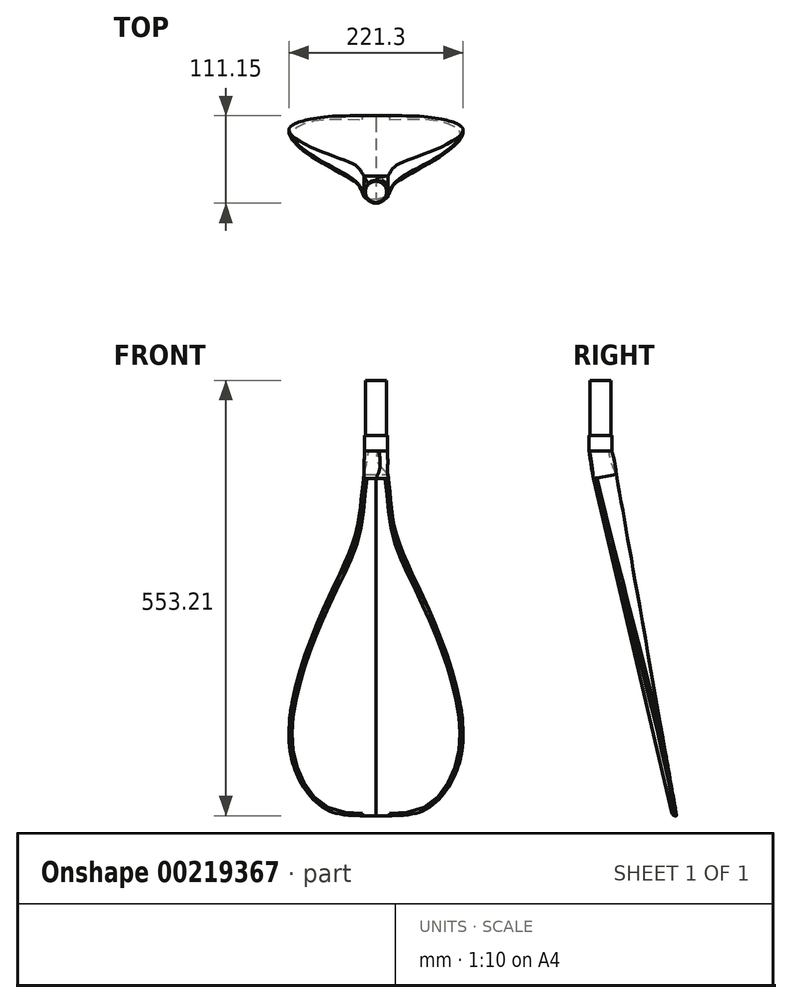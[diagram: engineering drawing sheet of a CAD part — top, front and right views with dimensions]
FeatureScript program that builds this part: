
annotation { "Feature Type Name" : "Feature", "Feature Type Description" : "" }
export const myFeature = defineFeature(function(context is Context, id is Id, definition is map)
    precondition{}
    {
        {
            var Q0;
            Q0=qCreatedBy(makeId("Top.planeOp"),FACE);
            cPlane(context, id + "F0", {"entities" : qUnion([Q0]), "cplaneType" : CPlaneType.OFFSET, "offset" : 500 * mm, "width" : 150 * mm, "height" : 150 * mm});
        }
        {
            var Q0;
            Q0=qCreatedBy(id+"F0.planeOp",FACE);
            var sketch = newSketch(context, id + "F1", { "sketchPlane" : qUnion([Q0])});
            skCircle(sketch, "E0", {"center": v(0, 0) * mm, "radius": 14.5 * mm});
            skSolve(sketch);
        }
        {
            var Q0;
            Q0 = qSketchRegion(id + "F1", true);
            extrude(context, id + "F2", {"entities" : qUnion([Q0]), "oppositeDirection" : true, "depth" : 20 * mm});
        }
        {
            var Q0;
            Q0=qCreatedBy(makeId("Right.planeOp"),FACE);
            var sketch = newSketch(context, id + "F3", { "sketchPlane" : qUnion([Q0])});
            skLineSegment(sketch, "E1", {"start": v(0, 500) * mm, "end": v(0, 450) * mm});
            skLineSegment(sketch, "E2", {"start": v(0, 450) * mm, "end": v(79.35, 0) * mm});
            skSolve(sketch);
        }
        {
            var Q0;
            Q0=sQuery(id+"F3.wireOp",EDGE,"E2");
            cPlane(context, id + "F4", {"entities" : qUnion([Q0]), "cplaneType" : CPlaneType.LINE_ANGLE, "offset" : 25 * mm, "angle" : 90 * degree, "width" : 150 * mm, "height" : 150 * mm});
        }
        {
            var Q0;
            Q0=qCreatedBy(id+"F4.planeOp",FACE);
            var sketch = newSketch(context, id + "F5", { "sketchPlane" : qUnion([Q0])});
            skLineSegment(sketch, "E3.bottom", {"start": v(115, 440) * mm, "end": v(-115, 440) * mm});
            skLineSegment(sketch, "E3.top", {"start": v(115, 0) * mm, "end": v(-115, 0) * mm});
            skLineSegment(sketch, "E3.left", {"start": v(115, 440) * mm, "end": v(115, 0) * mm});
            skLineSegment(sketch, "E3.right", {"start": v(-115, 440) * mm, "end": v(-115, 0) * mm});
            skSolve(sketch);
        }
        {
            var Q0;
            Q0=makeQuery(id+"F5.imprint","IMPRINT",FACE,{"disambiguationData":[TD([[makeQuery(id+"F5.imprint","IMPRINT",EDGE,{"derivedFrom":sQuery(id+"F5.wireOp",EDGE,"E3.bottom")}),1.0]])]});
            extrude(context, id + "F6", {"entities" : qUnion([Q0]), "endBound" : BoundingType.SYMMETRIC, "depth" : 40 * mm});
        }
        {
            var Q0;
            Q0=makeQuery(id+"F6.opExtrude","CAP_FACE",FACE,{"disambiguationData":[OSD([sQuery(id+"F5.wireOp",EDGE,"E3.bottom"),sQuery(id+"F5.wireOp",EDGE,"E3.top"),sQuery(id+"F5.wireOp",EDGE,"E3.left"),sQuery(id+"F5.wireOp",EDGE,"E3.right")])],"isStart":false});
            var sketch = newSketch(context, id + "F7", { "sketchPlane" : qUnion([Q0])});
            skFitSpline(sketch, "E4", {"points": [v(0, 0) * mm, v(68.3, 10.67) * mm, v(110, 90.6) * mm, v(66.39, 268.32) * mm, v(26.77, 359.9) * mm, v(18, 415.25) * mm, v(15.5, 440) * mm], "startDerivative": vector(665.27, 0) * mm, "endDerivative": vector(0, 86.17) * mm});
            skFitSpline(sketch, "E5.MirrorCS", {"points": [v(0, 0) * mm, v(-68.3, 10.67) * mm, v(-110, 90.6) * mm, v(-66.39, 268.32) * mm, v(-26.77, 359.9) * mm, v(-18, 415.25) * mm, v(-15.5, 440) * mm], "startDerivative": vector(-665.27, 0) * mm, "endDerivative": vector(0, 86.17) * mm});
            skSolve(sketch);
        }
        {
            var Q0;
            {var subQ5=makeQuery(id+"F6.opExtrude","CAP_EDGE",EDGE,{"disambiguationData":[OSD([sQuery(id+"F5.wireOp",EDGE,"E3.left")])],"isStart":false});Q0=makeQuery(id+"F7.imprint","IMPRINT",FACE,{"disambiguationData":[TD([[makeQuery(id+"F7.imprint","IMPRINT",EDGE,{"derivedFrom":subQ5}),-1.0]])]});}
            var Q1;
            {var subQ5=makeQuery(id+"F6.opExtrude","CAP_EDGE",EDGE,{"disambiguationData":[OSD([sQuery(id+"F5.wireOp",EDGE,"E3.right")])],"isStart":false});Q1=makeQuery(id+"F7.imprint","IMPRINT",FACE,{"disambiguationData":[TD([[makeQuery(id+"F7.imprint","IMPRINT",EDGE,{"derivedFrom":subQ5}),1.0]])]});}
            extrude(context, id + "F8", {"entities" : qUnion([Q0, Q1]), "operationType" : NewBodyOperationType.REMOVE, "endBound" : BoundingType.THROUGH_ALL, "oppositeDirection" : true, "depth" : 25 * mm});
        }
        {
            var Q0;
            Q0=qCreatedBy(makeId("Right.planeOp"),FACE);
            var sketch = newSketch(context, id + "F9", { "sketchPlane" : qUnion([Q0])});
            skLineSegment(sketch, "E6", {"start": v(-9.15, 445.17) * mm, "end": v(91.73, 16.17) * mm});
            skLineSegment(sketch, "E7", {"start": v(-9.15, 445.17) * mm, "end": v(-62.33, 445.17) * mm});
            skLineSegment(sketch, "E8", {"start": v(-62.33, 445.17) * mm, "end": v(-62.33, 0) * mm});
            skLineSegment(sketch, "E9", {"start": v(-62.33, 0) * mm, "end": v(89.1, 0) * mm});
            skLineSegment(sketch, "E10", {"start": v(89.1, 0) * mm, "end": v(91.73, 16.17) * mm});
            skSolve(sketch);
        }
        {
            var Q0;
            Q0 = qSketchRegion(id + "F9", true);
            extrude(context, id + "F10", {"entities" : qUnion([Q0]), "operationType" : NewBodyOperationType.REMOVE, "endBound" : BoundingType.SYMMETRIC, "oppositeDirection" : true, "depth" : 230 * mm, "hasDraft" : true, "draftAngle" : 3 * degree});
        }
        {
            var Q0;
            Q0=makeQuery(id+"F8.boolean.opBoolean","COPY",EDGE,{"derivedFrom":makeQuery(id+"F8.opExtrude","CAP_EDGE",EDGE,{"disambiguationData":[OSD([sQuery(id+"F7.wireOp",EDGE,"E4")])],"isStart":true})});
            var Q1;
            Q1=makeQuery(id+"F8.boolean.opBoolean","COPY",EDGE,{"derivedFrom":makeQuery(id+"F8.opExtrude","CAP_EDGE",EDGE,{"disambiguationData":[OSD([sQuery(id+"F7.wireOp",EDGE,"E5.MirrorCS")])],"isStart":true})});
            var Q2;
            Q2=makeQuery(id+"F10.boolean.opBoolean","INTERSECT",EDGE,{"derivedFrom":[makeQuery(id+"F8.boolean.opBoolean","COPY",FACE,{"derivedFrom":makeQuery(id+"F8.opExtrude","SWEPT_FACE",FACE,{"disambiguationData":[OSD([sQuery(id+"F7.wireOp",EDGE,"E4")])]})}),makeQuery(id+"F10.split0.splitOp","SPLIT",FACE,{"derivedFrom":makeQuery(id+"F10.opExtrude","SWEPT_FACE",FACE,{"disambiguationData":[OSD([sQuery(id+"F9.wireOp",EDGE,"E6")])]})})]});
            var Q3;
            Q3=makeQuery(id+"F10.boolean.opBoolean","INTERSECT",EDGE,{"derivedFrom":[makeQuery(id+"F8.boolean.opBoolean","COPY",FACE,{"derivedFrom":makeQuery(id+"F8.opExtrude","SWEPT_FACE",FACE,{"disambiguationData":[OSD([sQuery(id+"F7.wireOp",EDGE,"E5.MirrorCS")])]})}),makeQuery(id+"F10.split0.splitOp","SPLIT",FACE,{"derivedFrom":makeQuery(id+"F10.opExtrude","SWEPT_FACE",FACE,{"disambiguationData":[OSD([sQuery(id+"F9.wireOp",EDGE,"E6")])]}),"isFromBackBody":true})]});
            fillet(context, id + "F11", {"entities" : qUnion([Q0, Q1, Q2, Q3]), "radius" : 4.1 * mm, "tangentPropagation" : true, "allowEdgeOverflow" : false});
        }
        {
            var Q0;
            {var subQ0=sQuery(id+"F7.wireOp",EDGE,"E4");Q0=makeQuery(id+"F11.opFillet","BLEND_EDGE",EDGE,{"disambiguationData":[OD(1.0)],"blendedFrom":[makeQuery(id+"F8.boolean.opBoolean","COPY",EDGE,{"derivedFrom":makeQuery(id+"F8.opExtrude","CAP_EDGE",EDGE,{"disambiguationData":[OSD([subQ0])],"isStart":true})}),makeQuery(id+"F10.boolean.opBoolean","INTERSECT",EDGE,{"derivedFrom":[makeQuery(id+"F8.boolean.opBoolean","COPY",FACE,{"derivedFrom":makeQuery(id+"F8.opExtrude","SWEPT_FACE",FACE,{"disambiguationData":[OSD([subQ0])]})}),makeQuery(id+"F10.split0.splitOp","SPLIT",FACE,{"derivedFrom":makeQuery(id+"F10.opExtrude","SWEPT_FACE",FACE,{"disambiguationData":[OSD([sQuery(id+"F9.wireOp",EDGE,"E6")])]})})]})],"blendedInto":[]});}
            var Q1;
            {var subQ0=sQuery(id+"F7.wireOp",EDGE,"E5.MirrorCS");Q1=makeQuery(id+"F11.opFillet","BLEND_EDGE",EDGE,{"disambiguationData":[OD(1.0)],"blendedFrom":[makeQuery(id+"F8.boolean.opBoolean","COPY",EDGE,{"derivedFrom":makeQuery(id+"F8.opExtrude","CAP_EDGE",EDGE,{"disambiguationData":[OSD([subQ0])],"isStart":true})}),makeQuery(id+"F10.boolean.opBoolean","INTERSECT",EDGE,{"derivedFrom":[makeQuery(id+"F8.boolean.opBoolean","COPY",FACE,{"derivedFrom":makeQuery(id+"F8.opExtrude","SWEPT_FACE",FACE,{"disambiguationData":[OSD([subQ0])]})}),makeQuery(id+"F10.split0.splitOp","SPLIT",FACE,{"derivedFrom":makeQuery(id+"F10.opExtrude","SWEPT_FACE",FACE,{"disambiguationData":[OSD([sQuery(id+"F9.wireOp",EDGE,"E6")])]}),"isFromBackBody":true})]})],"blendedInto":[]});}
            var Q2;
            {var subQ0=sQuery(id+"F7.wireOp",EDGE,"E4");Q2=makeQuery(id+"F11.opFillet","BLEND_EDGE",EDGE,{"disambiguationData":[OD(0.0)],"blendedFrom":[makeQuery(id+"F8.boolean.opBoolean","COPY",EDGE,{"derivedFrom":makeQuery(id+"F8.opExtrude","CAP_EDGE",EDGE,{"disambiguationData":[OSD([subQ0])],"isStart":true})}),makeQuery(id+"F10.boolean.opBoolean","INTERSECT",EDGE,{"derivedFrom":[makeQuery(id+"F8.boolean.opBoolean","COPY",FACE,{"derivedFrom":makeQuery(id+"F8.opExtrude","SWEPT_FACE",FACE,{"disambiguationData":[OSD([subQ0])]})}),makeQuery(id+"F10.split0.splitOp","SPLIT",FACE,{"derivedFrom":makeQuery(id+"F10.opExtrude","SWEPT_FACE",FACE,{"disambiguationData":[OSD([sQuery(id+"F9.wireOp",EDGE,"E6")])]})})]})],"blendedInto":[]});}
            var Q3;
            Q3=makeQuery(id+"F11.opFillet","BLEND_EDGE",EDGE,{"blendedFrom":[makeQuery(id+"F8.boolean.opBoolean","COPY",EDGE,{"derivedFrom":makeQuery(id+"F8.opExtrude","CAP_EDGE",EDGE,{"disambiguationData":[OSD([sQuery(id+"F7.wireOp",EDGE,"E4")])],"isStart":true})}),makeQuery(id+"F10.boolean.opBoolean","INTERSECT",EDGE,{"derivedFrom":[makeQuery(id+"F8.boolean.opBoolean","COPY",FACE,{"derivedFrom":makeQuery(id+"F8.opExtrude","SWEPT_FACE",FACE,{"disambiguationData":[OSD([sQuery(id+"F7.wireOp",EDGE,"E5.MirrorCS")])]})}),makeQuery(id+"F10.split0.splitOp","SPLIT",FACE,{"derivedFrom":makeQuery(id+"F10.opExtrude","SWEPT_FACE",FACE,{"disambiguationData":[OSD([sQuery(id+"F9.wireOp",EDGE,"E6")])]}),"isFromBackBody":true})]})],"blendedInto":[]});
            fillet(context, id + "F12", {"entities" : qUnion([Q0, Q1, Q2, Q3]), "radius" : 1.1 * mm, "tangentPropagation" : true, "allowEdgeOverflow" : false});
        }
        {
            var Q0;
            Q0=makeQuery(id+"F6.opExtrude","SWEPT_FACE",FACE,{"disambiguationData":[OSD([sQuery(id+"F5.wireOp",EDGE,"E3.bottom")])]});
            cPlane(context, id + "F13", {"entities" : qUnion([Q0]), "cplaneType" : CPlaneType.OFFSET, "offset" : 20 * mm, "width" : 150 * mm, "height" : 150 * mm});
        }
        {
            var Q0;
            Q0=qCreatedBy(id+"F13.planeOp",FACE);
            var sketch = newSketch(context, id + "F14", { "sketchPlane" : qUnion([Q0])});
            skCircle(sketch, "E11", {"center": v(0, 83.6) * mm, "radius": 15 * mm});
            skSolve(sketch);
        }
        {
            var Q0;
            Q0=qCreatedBy(makeId("Right.planeOp"),FACE);
            var sketch = newSketch(context, id + "F15", { "sketchPlane" : qUnion([Q0])});
            skFitSpline(sketch, "E12", {"points": [v(-9.28, 445.11) * mm, v(-12.88, 464.2) * mm, v(-14.36, 479.97) * mm], "startDerivative": vector(-9.98, 45.05) * mm, "endDerivative": vector(0.77, 15.87) * mm});
            skSolve(sketch);
        }
        {
            var Q0;
            Q0=makeQuery(id+"F6.opExtrude","SWEPT_FACE",FACE,{"disambiguationData":[OSD([sQuery(id+"F5.wireOp",EDGE,"E3.bottom")])]});
            var Q1;
            Q1=makeQuery(id+"F14.imprint","IMPRINT",FACE,{"disambiguationData":[TD([[makeQuery(id+"F14.imprint","IMPRINT",EDGE,{"derivedFrom":sQuery(id+"F14.wireOp",EDGE,"E11")}),1.0]])]});
            var Q2;
            Q2=makeQuery(id+"F2.opExtrude","CAP_FACE",FACE,{"disambiguationData":[OSD([sQuery(id+"F1.wireOp",EDGE,"E0")])],"isStart":false});
            var Q3;
            Q3=sQuery(id+"F15.wireOp",EDGE,"E12");
            loft(context, id + "F16", {"sheetProfilesArray" : [{ "sheetProfileEntities" : qUnion([Q0]) }, { "sheetProfileEntities" : qUnion([Q1]) }, { "sheetProfileEntities" : qUnion([Q2]) }], "guidesArray" : [{ "guideEntities" : qUnion([Q3]), "guideDerivativeType" : LoftGuideDerivativeType.DEFAULT, "guideDerivativeMagnitude" : 1 }]});
        }
        {
            var Q0;
            Q0=makeQuery(id+"F2.opExtrude","CAP_FACE",FACE,{"disambiguationData":[OSD([sQuery(id+"F1.wireOp",EDGE,"E0")])],"isStart":true});
            var sketch = newSketch(context, id + "F17", { "sketchPlane" : qUnion([Q0])});
            skCircle(sketch, "E13", {"center": v(0, 0) * mm, "radius": 13.5 * mm});
            skSolve(sketch);
        }
        {
            var Q0;
            Q0 = qSketchRegion(id + "F17", true);
            extrude(context, id + "F18", {"entities" : qUnion([Q0]), "operationType" : NewBodyOperationType.ADD, "depth" : 70 * mm});
        }
    });
